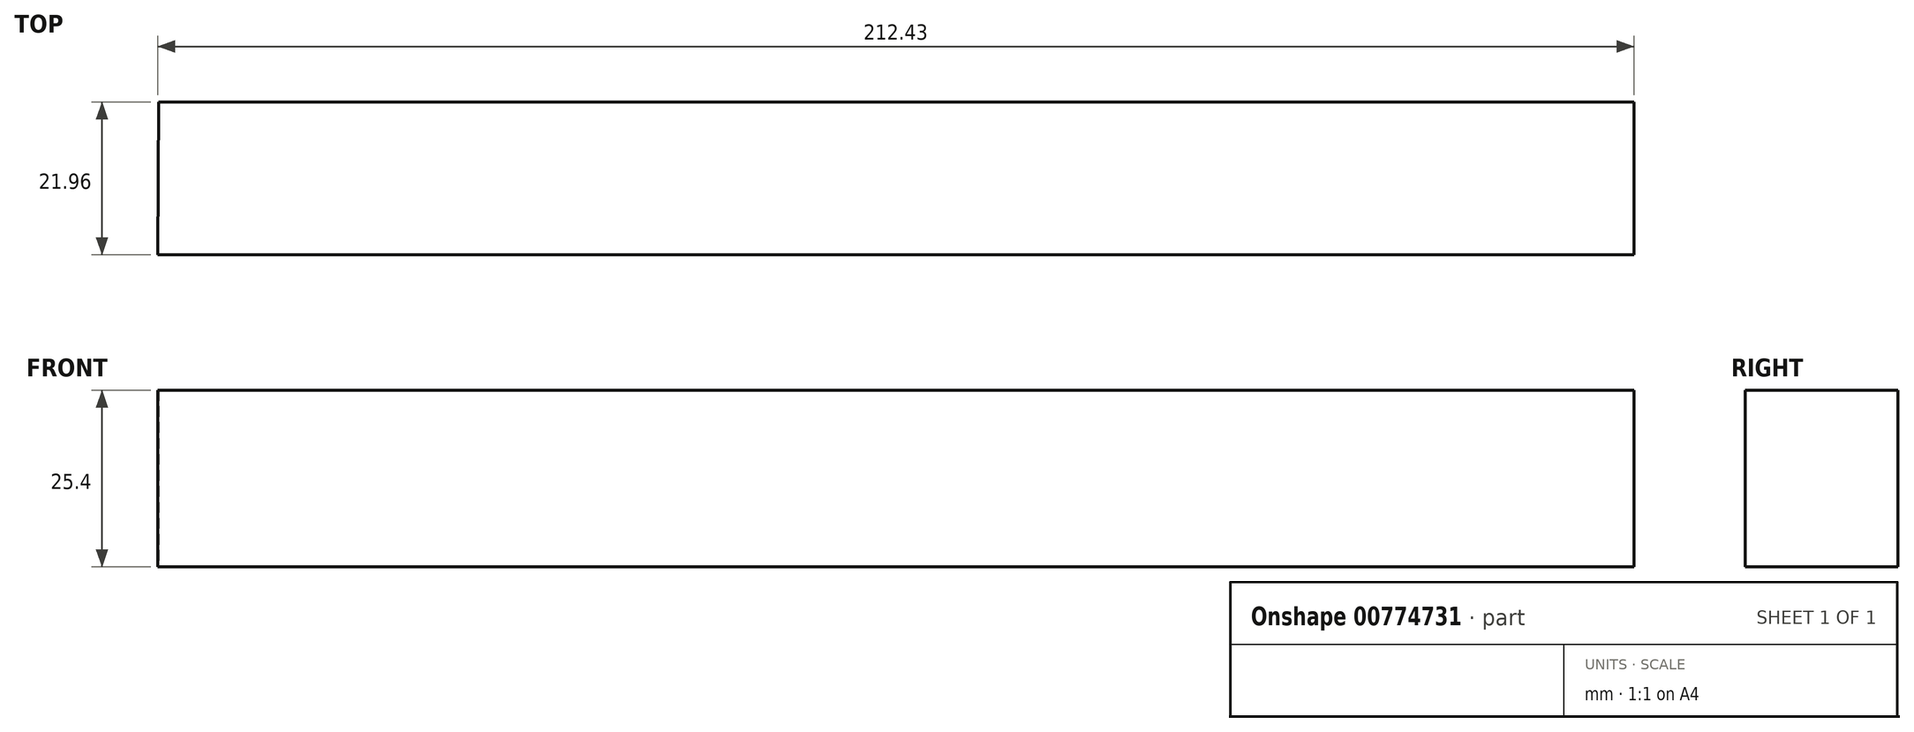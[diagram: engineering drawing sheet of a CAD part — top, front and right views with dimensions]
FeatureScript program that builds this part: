
annotation { "Feature Type Name" : "Feature", "Feature Type Description" : "" }
export const myFeature = defineFeature(function(context is Context, id is Id, definition is map)
    precondition{}
    {
        {
            var Q0;
            Q0=qCreatedBy(makeId("Top.planeOp"),FACE);
            var sketch = newSketch(context, id + "F0", { "sketchPlane" : qUnion([Q0])});
            skLineSegment(sketch, "E0", {"start": v(-121.94, -42.94) * mm, "end": v(90.49, -42.94) * mm});
            skLineSegment(sketch, "E1", {"start": v(90.49, -20.98) * mm, "end": v(-121.76, -20.98) * mm});
            skLineSegment(sketch, "E2", {"start": v(-121.76, -20.98) * mm, "end": v(-121.94, -42.94) * mm});
            skLineSegment(sketch, "E3", {"start": v(90.49, -20.98) * mm, "end": v(90.49, -42.94) * mm});
            skSolve(sketch);
        }
        {
            var Q0;
            Q0 = qSketchRegion(id + "F0", true);
            extrude(context, id + "F1", {"entities" : qUnion([Q0]), "depth" : 25.4 * mm, "offsetDistance" : 25.4 * mm});
        }
    });
